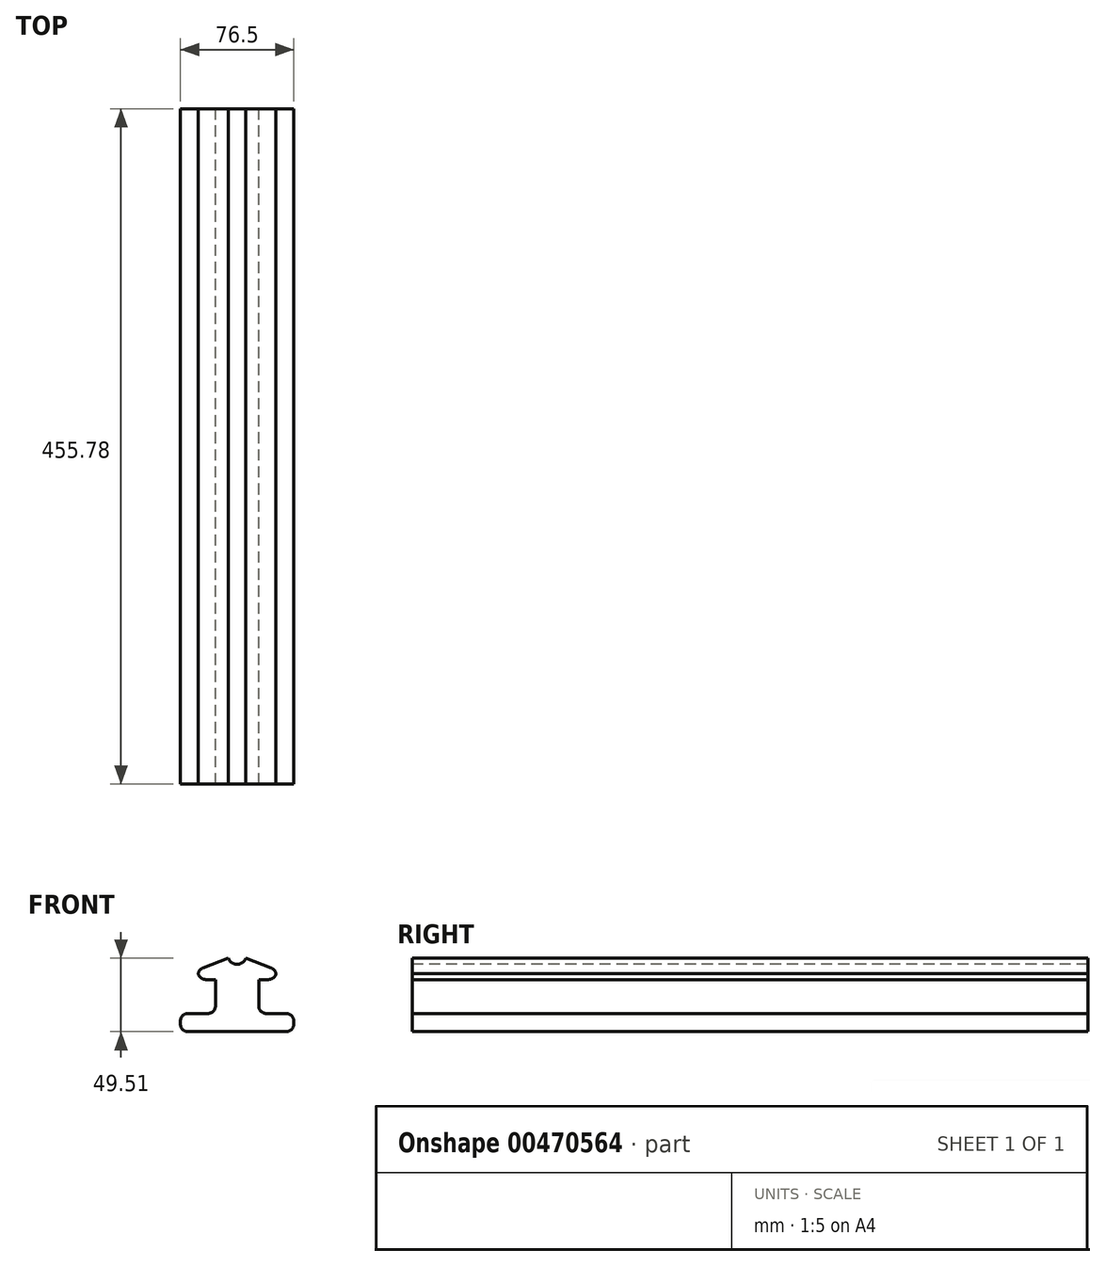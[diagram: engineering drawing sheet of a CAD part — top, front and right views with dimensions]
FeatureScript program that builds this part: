
annotation { "Feature Type Name" : "Feature", "Feature Type Description" : "" }
export const myFeature = defineFeature(function(context is Context, id is Id, definition is map)
    precondition{}
    {
        {
            var Q0;
            Q0=qCreatedBy(makeId("Front.planeOp"),FACE);
            var sketch = newSketch(context, id + "F0", { "sketchPlane" : qUnion([Q0])});
            skLineSegment(sketch, "E0", {"start": v(0, 0) * mm, "end": v(38.25, 0) * mm});
            skLineSegment(sketch, "E1", {"start": v(38.25, 0) * mm, "end": v(38.25, 12.27) * mm});
            skLineSegment(sketch, "E2", {"start": v(38.25, 12.27) * mm, "end": v(14.62, 12.27) * mm});
            skLineSegment(sketch, "E3", {"start": v(14.62, 12.27) * mm, "end": v(14.62, 35.19) * mm});
            skLineSegment(sketch, "E4", {"start": v(14.62, 35.19) * mm, "end": v(26.34, 35.19) * mm});
            skLineSegment(sketch, "E5", {"start": v(26.34, 35.19) * mm, "end": v(26.34, 41.68) * mm});
            skLineSegment(sketch, "E6", {"start": v(26.34, 41.68) * mm, "end": v(0, 51.79) * mm});
            skLineSegment(sketch, "E7.MirrorCS", {"start": v(-26.34, 41.68) * mm, "end": v(0, 51.79) * mm});
            skLineSegment(sketch, "E8.MirrorCS", {"start": v(-14.62, 12.27) * mm, "end": v(-14.62, 35.19) * mm});
            skLineSegment(sketch, "E9.MirrorCS", {"start": v(-14.62, 35.19) * mm, "end": v(-26.34, 35.19) * mm});
            skLineSegment(sketch, "E10.MirrorCS", {"start": v(-38.25, 12.27) * mm, "end": v(-14.62, 12.27) * mm});
            skLineSegment(sketch, "E11.MirrorCS", {"start": v(0, 0) * mm, "end": v(-38.25, 0) * mm});
            skLineSegment(sketch, "E12.MirrorCS", {"start": v(-38.25, 0) * mm, "end": v(-38.25, 12.27) * mm});
            skLineSegment(sketch, "E13.MirrorCS", {"start": v(-26.34, 35.19) * mm, "end": v(-26.34, 41.68) * mm});
            skPoint(sketch, "E14", {"position": v(0, 51.79) * mm});
            skPoint(sketch, "E15", {"position": v(38.4, 100.51) * mm});
            skPoint(sketch, "E16", {"position": v(0, 64.02) * mm});
            skSolve(sketch);
        }
        {
            var Q0;
            Q0=makeQuery(id+"F0.imprint","IMPRINT",FACE,{"disambiguationData":[TD([[makeQuery(id+"F0.imprint","IMPRINT",EDGE,{"derivedFrom":sQuery(id+"F0.wireOp",EDGE,"E0")}),1.0]])]});
            extrude(context, id + "F1", {"entities" : qUnion([Q0]), "endBound" : BoundingType.SYMMETRIC, "depth" : 455.78 * mm});
        }
        {
            var Q0;
            Q0=makeQuery(id+"F1.opExtrude","CAP_FACE",FACE,{"disambiguationData":[OSD([sQuery(id+"F0.wireOp",EDGE,"E0"),sQuery(id+"F0.wireOp",EDGE,"E1"),sQuery(id+"F0.wireOp",EDGE,"E2"),sQuery(id+"F0.wireOp",EDGE,"E3"),sQuery(id+"F0.wireOp",EDGE,"E4"),sQuery(id+"F0.wireOp",EDGE,"E5"),sQuery(id+"F0.wireOp",EDGE,"E6"),sQuery(id+"F0.wireOp",EDGE,"E7.MirrorCS"),sQuery(id+"F0.wireOp",EDGE,"E8.MirrorCS"),sQuery(id+"F0.wireOp",EDGE,"E9.MirrorCS"),sQuery(id+"F0.wireOp",EDGE,"E10.MirrorCS"),sQuery(id+"F0.wireOp",EDGE,"E11.MirrorCS"),sQuery(id+"F0.wireOp",EDGE,"E12.MirrorCS"),sQuery(id+"F0.wireOp",EDGE,"E13.MirrorCS")])],"isStart":false});
            var sketch = newSketch(context, id + "F2", { "sketchPlane" : qUnion([Q0])});
            skCircle(sketch, "E17", {"center": v(0, 51.79) * mm, "radius": 4.77 * mm});
            skSolve(sketch);
        }
        {
            var Q0;
            Q0=sQuery(id+"F2.wireOp",VERTEX,"E17.center");
            var Q1;
            Q1=makeQuery(id+"F1.opExtrude","SWEPT_BODY",BODY,{"disambiguationData":[OSD([sQuery(id+"F0.wireOp",EDGE,"E0"),sQuery(id+"F0.wireOp",EDGE,"E1"),sQuery(id+"F0.wireOp",EDGE,"E2"),sQuery(id+"F0.wireOp",EDGE,"E3"),sQuery(id+"F0.wireOp",EDGE,"E4"),sQuery(id+"F0.wireOp",EDGE,"E5"),sQuery(id+"F0.wireOp",EDGE,"E6"),sQuery(id+"F0.wireOp",EDGE,"E7.MirrorCS"),sQuery(id+"F0.wireOp",EDGE,"E8.MirrorCS"),sQuery(id+"F0.wireOp",EDGE,"E9.MirrorCS"),sQuery(id+"F0.wireOp",EDGE,"E10.MirrorCS"),sQuery(id+"F0.wireOp",EDGE,"E11.MirrorCS"),sQuery(id+"F0.wireOp",EDGE,"E12.MirrorCS"),sQuery(id+"F0.wireOp",EDGE,"E13.MirrorCS")])]});
            hole(context, id + "F3", {"style" : HoleStyle.SIMPLE, "endStyle" : HoleEndStyle.THROUGH, "holeDiameter" : 12.7 * mm, "isTappedThrough" : true, "tappedDepth" : 12.7 * mm, "tapClearance" : 3, "locations" : qUnion([Q0]), "scope" : qUnion([Q1])});
        }
        {
            var Q0;
            Q0=makeQuery(id+"F1.opExtrude","SWEPT_EDGE",EDGE,{"disambiguationData":[OSD([sQuery(id+"F0.wireOp",EDGE,"E5"),sQuery(id+"F0.wireOp",EDGE,"E6")])]});
            var Q1;
            Q1=makeQuery(id+"F3.hole-0.boolean.opBoolean","INTERSECT",EDGE,{"derivedFrom":[makeQuery(id+"F1.opExtrude","SWEPT_FACE",FACE,{"disambiguationData":[OSD([sQuery(id+"F0.wireOp",EDGE,"E6")])]}),makeQuery(id+"F3.hole-0.opRevolve","SWEPT_FACE",FACE,{"disambiguationData":[OSD([sQuery(id+"F3.hole-0.sketch.wireOp",EDGE,"core_line_2")])]})]});
            var Q2;
            Q2=makeQuery(id+"F3.hole-0.boolean.opBoolean","INTERSECT",EDGE,{"derivedFrom":[makeQuery(id+"F1.opExtrude","SWEPT_FACE",FACE,{"disambiguationData":[OSD([sQuery(id+"F0.wireOp",EDGE,"E7.MirrorCS")])]}),makeQuery(id+"F3.hole-0.opRevolve","SWEPT_FACE",FACE,{"disambiguationData":[OSD([sQuery(id+"F3.hole-0.sketch.wireOp",EDGE,"core_line_2")])]})]});
            var Q3;
            Q3=makeQuery(id+"F1.opExtrude","SWEPT_EDGE",EDGE,{"disambiguationData":[OSD([sQuery(id+"F0.wireOp",EDGE,"E4"),sQuery(id+"F0.wireOp",EDGE,"E5")])]});
            var Q4;
            Q4=makeQuery(id+"F1.opExtrude","SWEPT_EDGE",EDGE,{"disambiguationData":[OSD([sQuery(id+"F0.wireOp",EDGE,"E7.MirrorCS"),sQuery(id+"F0.wireOp",EDGE,"E13.MirrorCS")])]});
            var Q5;
            Q5=makeQuery(id+"F1.opExtrude","SWEPT_EDGE",EDGE,{"disambiguationData":[OSD([sQuery(id+"F0.wireOp",EDGE,"E9.MirrorCS"),sQuery(id+"F0.wireOp",EDGE,"E13.MirrorCS")])]});
            var Q6;
            Q6=makeQuery(id+"F1.opExtrude","SWEPT_EDGE",EDGE,{"disambiguationData":[OSD([sQuery(id+"F0.wireOp",EDGE,"E8.MirrorCS"),sQuery(id+"F0.wireOp",EDGE,"E10.MirrorCS")])]});
            var Q7;
            Q7=makeQuery(id+"F1.opExtrude","SWEPT_EDGE",EDGE,{"disambiguationData":[OSD([sQuery(id+"F0.wireOp",EDGE,"E2"),sQuery(id+"F0.wireOp",EDGE,"E3")])]});
            var Q8;
            Q8=makeQuery(id+"F1.opExtrude","SWEPT_EDGE",EDGE,{"disambiguationData":[OSD([sQuery(id+"F0.wireOp",EDGE,"E1"),sQuery(id+"F0.wireOp",EDGE,"E2")])]});
            var Q9;
            Q9=makeQuery(id+"F1.opExtrude","SWEPT_EDGE",EDGE,{"disambiguationData":[OSD([sQuery(id+"F0.wireOp",EDGE,"E0"),sQuery(id+"F0.wireOp",EDGE,"E1")])]});
            var Q10;
            Q10=makeQuery(id+"F1.opExtrude","SWEPT_EDGE",EDGE,{"disambiguationData":[OSD([sQuery(id+"F0.wireOp",EDGE,"E10.MirrorCS"),sQuery(id+"F0.wireOp",EDGE,"E12.MirrorCS")])]});
            var Q11;
            Q11=makeQuery(id+"F1.opExtrude","SWEPT_EDGE",EDGE,{"disambiguationData":[OSD([sQuery(id+"F0.wireOp",EDGE,"E11.MirrorCS"),sQuery(id+"F0.wireOp",EDGE,"E12.MirrorCS")])]});
            fillet(context, id + "F4", {"entities" : qUnion([Q0, Q1, Q2, Q3, Q4, Q5, Q6, Q7, Q8, Q9, Q10, Q11]), "radius" : 5.08 * mm, "tangentPropagation" : true, "allowEdgeOverflow" : false});
        }
    });
